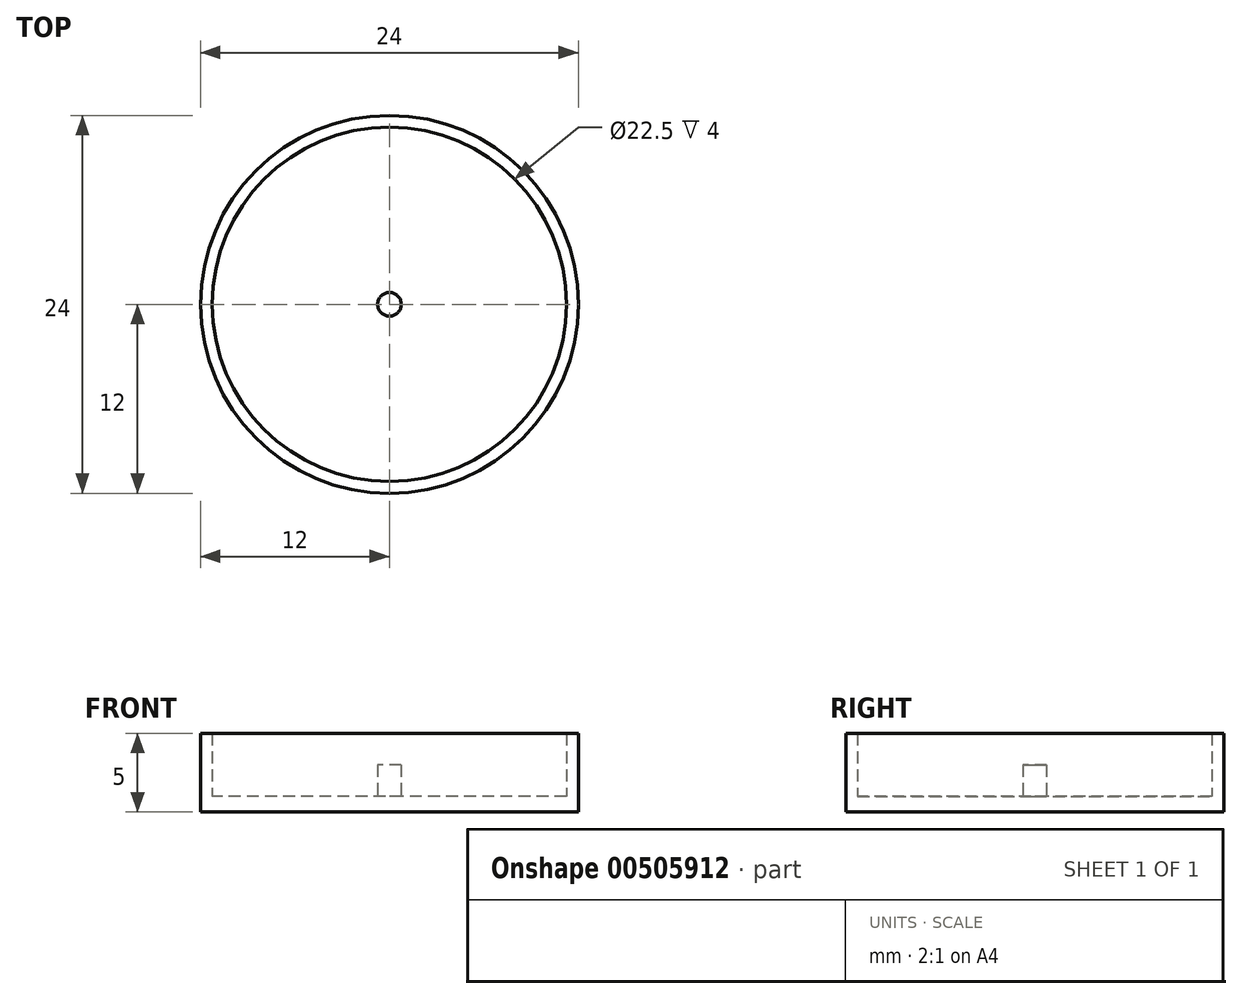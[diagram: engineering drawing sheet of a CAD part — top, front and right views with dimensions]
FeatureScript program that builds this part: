
annotation { "Feature Type Name" : "Feature", "Feature Type Description" : "" }
export const myFeature = defineFeature(function(context is Context, id is Id, definition is map)
    precondition{}
    {
        {
            var Q0;
            Q0=qCreatedBy(makeId("Top.planeOp"),FACE);
            var sketch = newSketch(context, id + "F0", { "sketchPlane" : qUnion([Q0])});
            skCircle(sketch, "E0", {"center": v(0, 0) * mm, "radius": 11.75 * mm});
            skSolve(sketch);
        }
        {
            var Q0;
            Q0 = qSketchRegion(id + "F0", true);
            extrude(context, id + "F1", {"entities" : qUnion([Q0]), "depth" : 1 * mm});
        }
        {
            var Q0;
            Q0=qCreatedBy(makeId("Top.planeOp"),FACE);
            var sketch = newSketch(context, id + "F2", { "sketchPlane" : qUnion([Q0])});
            skCircle(sketch, "E1", {"center": v(0, 0) * mm, "radius": 11.25 * mm});
            skCircle(sketch, "E2", {"center": v(0, 0) * mm, "radius": 12 * mm});
            skSolve(sketch);
        }
        {
            var Q0;
            Q0 = qSketchRegion(id + "F2", true);
            extrude(context, id + "F3", {"entities" : qUnion([Q0]), "operationType" : NewBodyOperationType.ADD, "depth" : 5 * mm});
        }
        {
            var Q0;
            Q0=qCreatedBy(makeId("Top.planeOp"),FACE);
            var sketch = newSketch(context, id + "F4", { "sketchPlane" : qUnion([Q0])});
            skCircle(sketch, "E3", {"center": v(0, 0) * mm, "radius": 0.75 * mm});
            skSolve(sketch);
        }
        {
            var Q0;
            Q0 = qSketchRegion(id + "F4", true);
            extrude(context, id + "F5", {"entities" : qUnion([Q0]), "operationType" : NewBodyOperationType.ADD, "depth" : 3 * mm});
        }
    });
